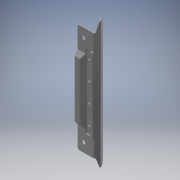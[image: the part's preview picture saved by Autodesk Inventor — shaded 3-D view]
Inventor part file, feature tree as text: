
AUTODESK INVENTOR PART (.ipt)
format: ipt  version: 2019 (Build 230136000, 136)  size: 851,968 bytes
history: native  units: mm
features: fillet x17, extrude x11, sketch x11, projected_geometry x6, mirror x4, plane x1, hole x1
ambient origin geometry x8: Origin, YZ Plane, XZ Plane, XY Plane, X Axis, Y Axis, Z Axis, Center Point
bodies: Solid1 (feature_tree)
feature tree (51):
  extrude  "Extrusion1"  Depth=2.001198mm
  extrude  "Extrusion2"  Depth=0.176244mm
  mirror  "Mirror1"
  extrude  "Extrusion3"  Depth=17.529399mm
  sketch  "Sketch5"  dims[d16=4.590825mm d17=4.753145mm]
  extrude  "Extrusion4"  Depth=4.753145mm
  extrude  "Extrusion5"  Depth=41.141792mm
  mirror  "Mirror2"
  plane  "Work Plane1"
  extrude  "Extrusion8"  Depth=56.25mm
  extrude  "Extrusion9"  Depth=8.386309mm
  extrude  "Extrusion10"  Depth=2.2mm
  mirror  "Mirror3"
  fillet  "Fillet29"  Radius=21.0mm
  fillet  "Fillet30"  Radius=60.0mm
  fillet  "Fillet32"  Radius=2.2mm
  fillet  "Fillet33"  Radius=2.2mm
  fillet  "Fillet34"  Radius=10.0mm
  fillet  "Fillet35"  Radius=2.2mm
  fillet  "Fillet36"  Radius=6.283185mm
  fillet  "Fillet39"  Radius=12.5mm
  fillet  "Fillet40"  Radius=24.692673mm
  fillet  "Fillet41"  Radius=23.549085mm
  extrude  "Extrusion11"  Depth=2.2mm
  extrude  "Extrusion12"  Depth=2.2mm
  fillet  "Fillet42"  Radius=2.2mm
  fillet  "Fillet43"  Radius=2.2mm
  fillet  "Fillet44"  Radius=2.502394mm
  fillet  "Fillet45"  Radius=2.356846mm
  mirror  "Mirror4"
  fillet  "Fillet46"  Radius=85.0mm
  fillet  "Fillet47"  Radius=2.2mm
  fillet  "Fillet48"  Radius=2.2mm
  hole  "Hole1"  [1 undecoded]
  extrude  "Extrusion13"  Depth=10.0mm
  sketch  "Sketch1"  dims[d5=15.669807mm d6=2.001198mm]
  sketch  "Sketch2"  dims[d12=0.273934mm d13=0.176244mm]
  sketch  "Sketch3"  dims[d14=13.529354mm d15=17.529399mm]
  sketch  "Sketch8"  dims[d18=30.56752mm d19=41.141792mm]
  projected_geometry  "Projected Loop2"
  projected_geometry  "Projected Loop3"
  projected_geometry  "Projected Loop4"
  sketch  "Sketch9"  dims[d20=7.901637mm d21=56.25mm]
  sketch  "Sketch10"  dims[d26=400.0mm d27=0.0mm d36=8.386309mm]
  sketch  "Sketch12"  dims[d41=3.0mm d42=5.2mm d49=21.0mm d50=0.0mm d52=60.0mm d53=2.2mm d54=56.25mm d55=2.2mm d58=10.0mm d59=0.0mm d62=2.2mm d63=6.283185mm d64=12.5mm d65=24.692673mm d66=0.0mm d67=23.549085mm d68=0.0mm]
  sketch  "Sketch13"  dims[d75=215.0mm d76=0.0mm d84=2.2mm]
  sketch  "Sketch14"  dims[d85=2.2mm d86=2.2mm d87=2.2mm d103=2.2mm d106=2.502394mm d107=2.356846mm d110=85.0mm d111=2.2mm d112=0.0mm d113=2.2mm d114=0.0mm]
  sketch  "Sketch15"  dims[d117=2.2mm d118=2.2mm d120=8.0mm d121=2.0mm d122=2.2mm d123=2.2mm d124=2.0mm d127=3.0mm d128=2.0mm d129=5.0mm d130=2.0mm d131=1.0mm d132=30.0mm d133=60.0mm d134=6.0mm d135=0.0mm d136=6.0mm d137=0.0mm d138=6.0mm d139=6.0mm d140=6.0mm d141=6.0mm d142=6.0mm d143=6.0mm d144=6.0mm d146=2.2mm d148=15.716326mm d149=5.2142mm d150=5.497787mm d151=15.0mm d152=142.15mm d153=37.993305mm d154=10.5mm d155=6.0mm d156=4.0mm d157=2.0mm d158=90.0deg d159=8.0mm d160=20.594885mm d161=90.0mm d162=23.808786mm d163=5.25mm d164=5.25mm d165=1.5mm d166=40.0mm d168=60.0mm d169=10.0mm d171=10.0mm d173=10.0mm d174=0.0mm]
  projected_geometry  "Project Cut Edges1"
  projected_geometry  "Project Cut Edges2"
  projected_geometry  "Project Cut Edges3"
note: 1 required parameter value undecoded (feature->parameter linkage not recoverable at this tier; creation-order binding heuristic only, values carry confidence <= 0.55)
